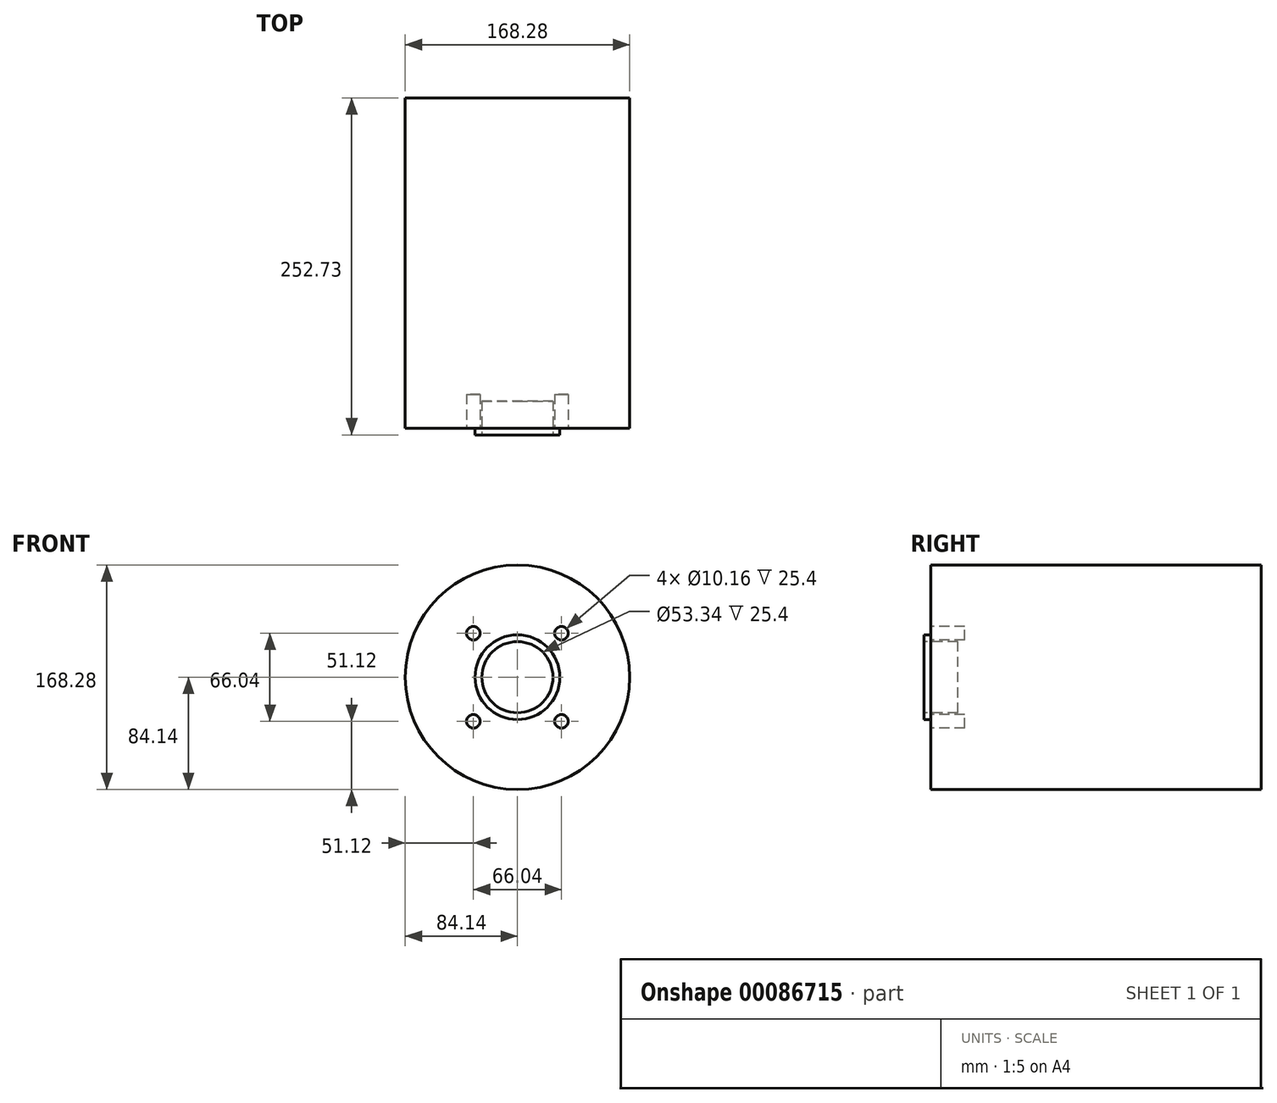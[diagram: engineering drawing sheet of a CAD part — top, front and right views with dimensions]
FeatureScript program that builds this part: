
annotation { "Feature Type Name" : "Feature", "Feature Type Description" : "" }
export const myFeature = defineFeature(function(context is Context, id is Id, definition is map)
    precondition{}
    {
        {
            var Q0;
            Q0=qCreatedBy(makeId("Front.planeOp"),FACE);
            var sketch = newSketch(context, id + "F0", { "sketchPlane" : qUnion([Q0])});
            skCircle(sketch, "E0", {"center": v(0, 0) * mm, "radius": 84.14 * mm});
            skSolve(sketch);
        }
        {
            var Q0;
            Q0=makeQuery(id+"F0.imprint","IMPRINT",FACE,{"disambiguationData":[TD([[makeQuery(id+"F0.imprint","IMPRINT",EDGE,{"derivedFrom":sQuery(id+"F0.wireOp",EDGE,"E0")}),1.0]])]});
            var Q1;
            Q1 = qSketchRegion(id + "F2", true);
            extrude(context, id + "F1", {"entities" : qUnion([Q0, Q1]), "depth" : 247.65 * mm});
        }
        {
            var Q0;
            Q0=makeQuery(id+"F1.opExtrude","CAP_FACE",FACE,{"disambiguationData":[OSD([sQuery(id+"F0.wireOp",EDGE,"E0")])],"isStart":false});
            var sketch = newSketch(context, id + "F2", { "sketchPlane" : qUnion([Q0])});
            skCircle(sketch, "E1", {"center": v(0, 0) * mm, "radius": 31.75 * mm});
            skSolve(sketch);
        }
        {
            var Q0;
            Q0=makeQuery(id+"F2.imprint","IMPRINT",FACE,{"disambiguationData":[TD([[makeQuery(id+"F2.imprint","IMPRINT",EDGE,{"derivedFrom":sQuery(id+"F2.wireOp",EDGE,"E1")}),1.0]])]});
            extrude(context, id + "F3", {"entities" : qUnion([Q0]), "operationType" : NewBodyOperationType.ADD, "depth" : 5.08 * mm});
        }
        {
            var Q0;
            Q0=makeQuery(id+"F1.opExtrude","CAP_FACE",FACE,{"disambiguationData":[OSD([sQuery(id+"F0.wireOp",EDGE,"E0")])],"isStart":false});
            var sketch = newSketch(context, id + "F4", { "sketchPlane" : qUnion([Q0])});
            skLineSegment(sketch, "E2.bottom", {"start": v(-38.1, 38.1) * mm, "end": v(38.1, 38.1) * mm});
            skLineSegment(sketch, "E2.top", {"start": v(-38.1, -38.1) * mm, "end": v(38.1, -38.1) * mm});
            skLineSegment(sketch, "E2.left", {"start": v(-38.1, 38.1) * mm, "end": v(-38.1, -38.1) * mm});
            skLineSegment(sketch, "E2.right", {"start": v(38.1, 38.1) * mm, "end": v(38.1, -38.1) * mm});
            skPoint(sketch, "E2.middle", {"position": v(0, 0) * mm});
            skCircle(sketch, "E3", {"center": v(33.02, 33.02) * mm, "radius": 5.08 * mm});
            skCircle(sketch, "E4.1.0", {"center": v(-33.02, 33.02) * mm, "radius": 5.08 * mm});
            skCircle(sketch, "E4.2.0", {"center": v(-33.02, -33.02) * mm, "radius": 5.08 * mm});
            skCircle(sketch, "E4.3.0", {"center": v(33.02, -33.02) * mm, "radius": 5.08 * mm});
            skSolve(sketch);
        }
        {
            var Q0;
            {var subQ0=sQuery(id+"F4.wireOp",EDGE,"E4.1.0");var subQ1=makeQuery(id+"F4.imprint","INTERSECT",VERTEX,{"derivedFrom":[sQuery(id+"F4.wireOp",EDGE,"E2.bottom"),subQ0]});Q0=makeQuery(id+"F4.imprint","IMPRINT",FACE,{"disambiguationData":[TD([[makeQuery(id+"F4.imprint","IMPRINT",EDGE,{"disambiguationData":[TD([[subQ1,-1.0]])],"derivedFrom":subQ0}),1.0]])]});}
            var Q1;
            {var subQ0=sQuery(id+"F4.wireOp",EDGE,"E3");var subQ1=makeQuery(id+"F4.imprint","INTERSECT",VERTEX,{"derivedFrom":[sQuery(id+"F4.wireOp",EDGE,"E2.bottom"),subQ0]});Q1=makeQuery(id+"F4.imprint","IMPRINT",FACE,{"disambiguationData":[TD([[makeQuery(id+"F4.imprint","IMPRINT",EDGE,{"disambiguationData":[TD([[subQ1,1.0]])],"derivedFrom":subQ0}),1.0]])]});}
            var Q2;
            {var subQ0=sQuery(id+"F4.wireOp",EDGE,"E4.3.0");var subQ1=makeQuery(id+"F4.imprint","INTERSECT",VERTEX,{"derivedFrom":[sQuery(id+"F4.wireOp",EDGE,"E2.top"),subQ0]});Q2=makeQuery(id+"F4.imprint","IMPRINT",FACE,{"disambiguationData":[TD([[makeQuery(id+"F4.imprint","IMPRINT",EDGE,{"disambiguationData":[TD([[subQ1,-1.0]])],"derivedFrom":subQ0}),1.0]])]});}
            var Q3;
            {var subQ0=sQuery(id+"F4.wireOp",EDGE,"E4.2.0");var subQ1=makeQuery(id+"F4.imprint","INTERSECT",VERTEX,{"derivedFrom":[sQuery(id+"F4.wireOp",EDGE,"E2.top"),subQ0]});Q3=makeQuery(id+"F4.imprint","IMPRINT",FACE,{"disambiguationData":[TD([[makeQuery(id+"F4.imprint","IMPRINT",EDGE,{"disambiguationData":[TD([[subQ1,1.0]])],"derivedFrom":subQ0}),1.0]])]});}
            extrude(context, id + "F5", {"entities" : qUnion([Q0, Q1, Q2, Q3]), "operationType" : NewBodyOperationType.REMOVE, "oppositeDirection" : true, "depth" : 25.4 * mm});
        }
        {
            var Q0;
            Q0=makeQuery(id+"F3.opExtrude","CAP_FACE",FACE,{"disambiguationData":[OSD([sQuery(id+"F2.wireOp",EDGE,"E1")])],"isStart":false});
            var sketch = newSketch(context, id + "F6", { "sketchPlane" : qUnion([Q0])});
            skCircle(sketch, "E5", {"center": v(0, 0) * mm, "radius": 26.67 * mm});
            skSolve(sketch);
        }
        {
            var Q0;
            Q0=makeQuery(id+"F6.imprint","IMPRINT",FACE,{"disambiguationData":[TD([[makeQuery(id+"F6.imprint","IMPRINT",EDGE,{"derivedFrom":sQuery(id+"F6.wireOp",EDGE,"E5")}),1.0]])]});
            extrude(context, id + "F7", {"entities" : qUnion([Q0]), "operationType" : NewBodyOperationType.REMOVE, "oppositeDirection" : true, "depth" : 25.4 * mm});
        }
    });
